# Revit family: 111212002203286
name_source: partatom
category: Modelos genéricos
revit_build: Autodesk Revit 2018 (Build: 20190510_1515(x64)
units: mm (PartAtom-declared; Revit-internal decimal feet)

## family parameters
Compartido = No
Corte con vacíos al cargar = No
Cota de conector redondo = Diámetro de uso
Puede alojar armadura = No
Punto de cálculo de habitación = No
Se basa en plano de trabajo = No
Siempre vertical = No
Tipo de pieza = Normal

## types (1)
- TOPE DE PUERTA ESFERICO PVC CAFE BOLSA 100UN
    Aplicacion = En piso como tope de puerta.
    Color = Cafe
    Descripción = Tope de puerta esférico.
    Dimension = 30 mm  [stored 0.0984252 ft]
    Empresa = CNP SPA.
    Espesor = 30 mm  [stored 0.0984252 ft]
    Largo = 0 mm  [stored 0 ft]
    Material = PVC flexible cafe
    Modelo = TOPE DE PUERTA ESFERICO
    Nombre SKU = TOPE DE PUERTA ESFERICO PVC CAFE BOLSA 100UN
    Num SKUs = 111212002203286
    URL = https://www.empresascnp.cl
    Unidad = Bolsas de 100 Unidades – Bolsas de 20 Unidades – Por Unidad
    Url Ficha tecnica = https://empresascnp.cl
    Uso = Se utiliza para evitar que las puertas tengan contacto con el muro, impidiendo que
esta le haga daño con los golpes.

note: [stored X ft] marks values corroborated as IEEE doubles in the binary element streams (Revit-internal decimal feet)

## geometry (parser evidence)
native form markers: Sweep x2
no freeform markers — native parametric forms only
